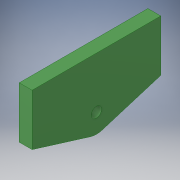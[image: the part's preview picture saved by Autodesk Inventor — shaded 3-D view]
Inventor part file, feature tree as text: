
AUTODESK INVENTOR PART (.ipt)
format: ipt  version: 2017 SP1 (Build 210196100, 196)  size: 97,280 bytes
history: native  units: in
note: dims shown in document units (in); Inventor stores cm internally (conversion verified against a paired STEP export)
features: extrude x1, sketch x1
ambient origin geometry x8: Origin, YZ Plane, XZ Plane, XY Plane, X Axis, Y Axis, Z Axis, Center Point
bodies: Solid1 (feature_tree)
feature tree (2):
  extrude  "Extrusion1"  Depth=0.25in
  sketch  "Sketch1"  dims[d0=0.2in d1=1.0in d2=0.493in d3=0.375in d4=2.5in d5=0.25in d6=0.0in]
